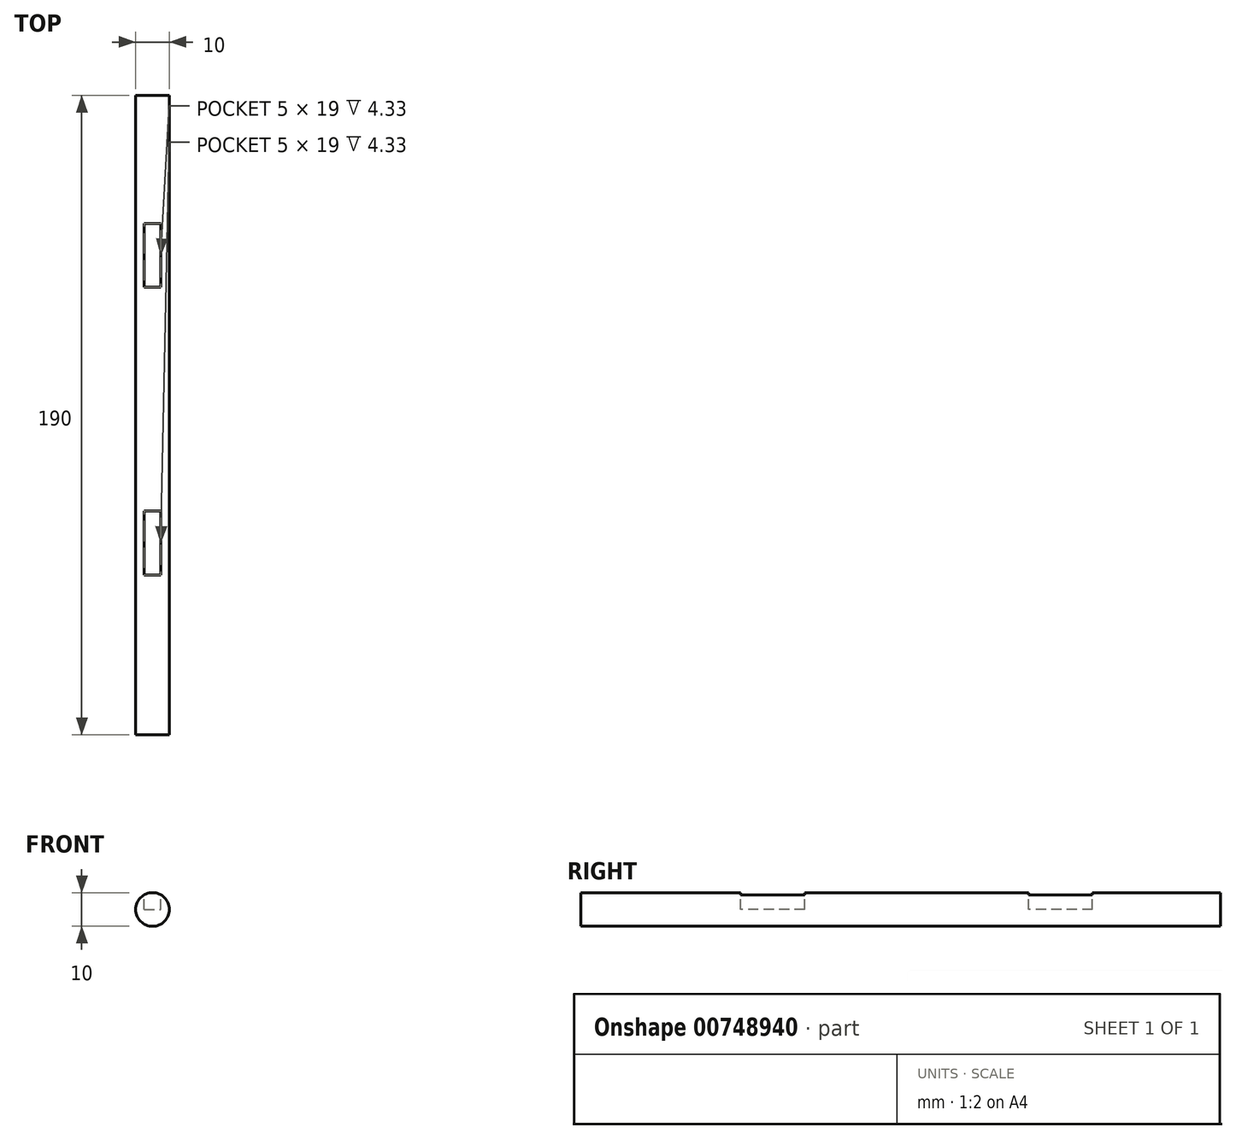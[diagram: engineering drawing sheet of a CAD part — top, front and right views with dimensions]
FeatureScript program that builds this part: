
annotation { "Feature Type Name" : "Feature", "Feature Type Description" : "" }
export const myFeature = defineFeature(function(context is Context, id is Id, definition is map)
    precondition{}
    {
        {
            var Q0;
            Q0=qCreatedBy(makeId("Front.planeOp"),FACE);
            var sketch = newSketch(context, id + "F0", { "sketchPlane" : qUnion([Q0])});
            skCircle(sketch, "E0", {"center": v(0, 0) * mm, "radius": 5 * mm});
            skSolve(sketch);
        }
        {
            var Q0;
            Q0 = qSketchRegion(id + "F0", true);
            extrude(context, id + "F1", {"entities" : qUnion([Q0]), "depth" : 190 * mm, "offsetDistance" : 25 * mm, "symmetric" : true});
        }
        {
            var Q0;
            Q0=qCreatedBy(makeId("Top.planeOp"),FACE);
            cPlane(context, id + "F2", {"entities" : qUnion([Q0]), "cplaneType" : CPlaneType.OFFSET, "offset" : 5 * mm, "width" : 150 * mm, "height" : 150 * mm});
        }
        {
            var Q0;
            Q0=qCreatedBy(id+"F2.planeOp",FACE);
            var sketch = newSketch(context, id + "F3", { "sketchPlane" : qUnion([Q0])});
            skLineSegment(sketch, "E1", {"start": v(0, 0) * mm, "end": v(0, -95) * mm});
            skLineSegment(sketch, "E2", {"start": v(0, -95) * mm, "end": v(0, -76) * mm});
            skLineSegment(sketch, "E3", {"start": v(0, 0) * mm, "end": v(0, 95) * mm});
            skLineSegment(sketch, "E4", {"start": v(0, 95) * mm, "end": v(0, 76) * mm});
            skLineSegment(sketch, "E5", {"start": v(0, 76) * mm, "end": v(0, -76) * mm});
            skLineSegment(sketch, "E6", {"start": v(0, 0) * mm, "end": v(0, 76) * mm});
            skLineSegment(sketch, "E7", {"start": v(0, 0) * mm, "end": v(0, -76) * mm});
            skLineSegment(sketch, "E8.bottom", {"start": v(-2.5, 57) * mm, "end": v(2.5, 57) * mm});
            skLineSegment(sketch, "E8.top", {"start": v(-2.5, 38) * mm, "end": v(2.5, 38) * mm});
            skLineSegment(sketch, "E8.left", {"start": v(-2.5, 57) * mm, "end": v(-2.5, 38) * mm});
            skLineSegment(sketch, "E8.right", {"start": v(2.5, 57) * mm, "end": v(2.5, 38) * mm});
            skPoint(sketch, "E8.middle", {"position": v(0, 47.5) * mm});
            skLineSegment(sketch, "E9", {"start": v(-53.81, 0) * mm, "end": v(-32.73, 0) * mm});
            skLineSegment(sketch, "E10.bottom", {"start": v(-2.5, -28.5) * mm, "end": v(2.5, -28.5) * mm});
            skLineSegment(sketch, "E10.top", {"start": v(-2.5, -47.5) * mm, "end": v(2.5, -47.5) * mm});
            skLineSegment(sketch, "E10.left", {"start": v(-2.5, -28.5) * mm, "end": v(-2.5, -47.5) * mm});
            skLineSegment(sketch, "E10.right", {"start": v(2.5, -28.5) * mm, "end": v(2.5, -47.5) * mm});
            skPoint(sketch, "E10.middle", {"position": v(0, -38) * mm});
            skSolve(sketch);
        }
        {
            var Q0;
            Q0 = qSketchRegion(id + "F3", true);
            extrude(context, id + "F4", {"entities" : qUnion([Q0]), "operationType" : NewBodyOperationType.REMOVE, "oppositeDirection" : true, "depth" : 5 * mm, "offsetDistance" : 25 * mm});
        }
    });
